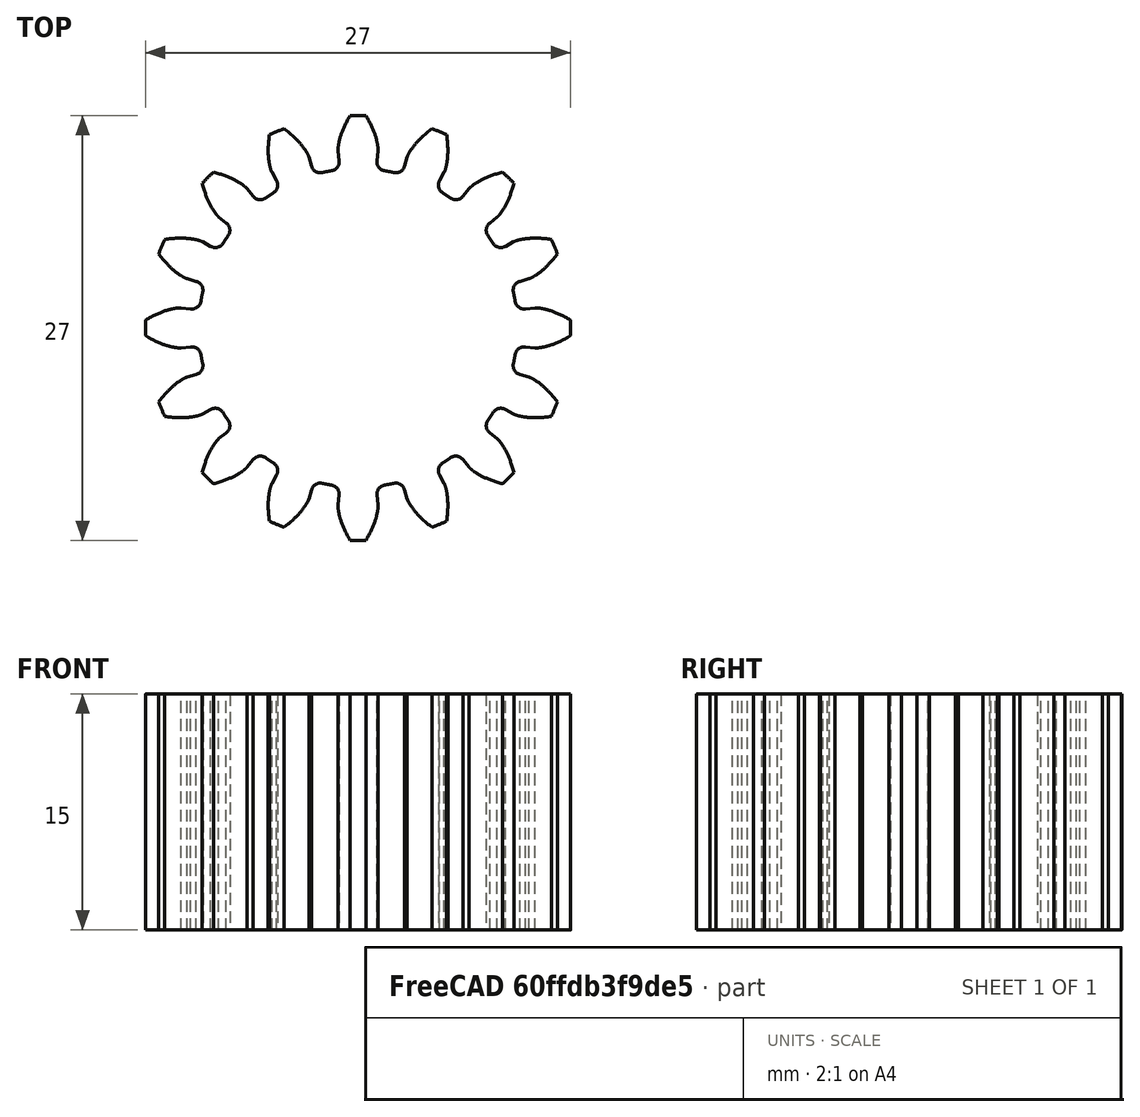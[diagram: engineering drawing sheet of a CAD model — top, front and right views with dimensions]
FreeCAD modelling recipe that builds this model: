
FCSTD DOCUMENT  (FreeCAD 1.0R39319 (Git))
Label: inv gear t16 m1_5 w15
License: All rights reserved
LicenseURL: https://en.wikipedia.org/wiki/All_rights_reserved
objects: Part::Part2DObjectPython×1, PartDesign::Pad×1, PartDesign::Body×1
note: 5 computed .brp shape members not serialized (recipe doc carries the construction recipe); baked Part::Feature solids carry a one-line shape summary decoded from their .brp

FEATURE [Part::Part2DObjectPython] InvoluteGear  # Draft 2D object (typed FeaturePython)
  AddendumCoefficient = 1
  DedendumCoefficient = 1.25
  ExternalGear = true
  HighPrecision = true
  Modules = 1.5
  NumberOfTeeth = 16
  PressureAngle = 20
  ProfileShiftCoefficient = 0
  RootFilletCoefficient = 0.38
FEATURE [PartDesign::Pad] Pad
  Direction = (0,0,1)
  Length = 15
  Length2 = 10
  Profile = -> InvoluteGear
  ReferenceAxis = -> InvoluteGear [N_Axis]
  Refine = true
  Suppressed = false
  Type = 0
FEATURE [PartDesign::Body] Body
  AllowCompound = false
  Group = -> [InvoluteGear,Pad]
  Origin = -> Origin
  Tip = -> Pad
